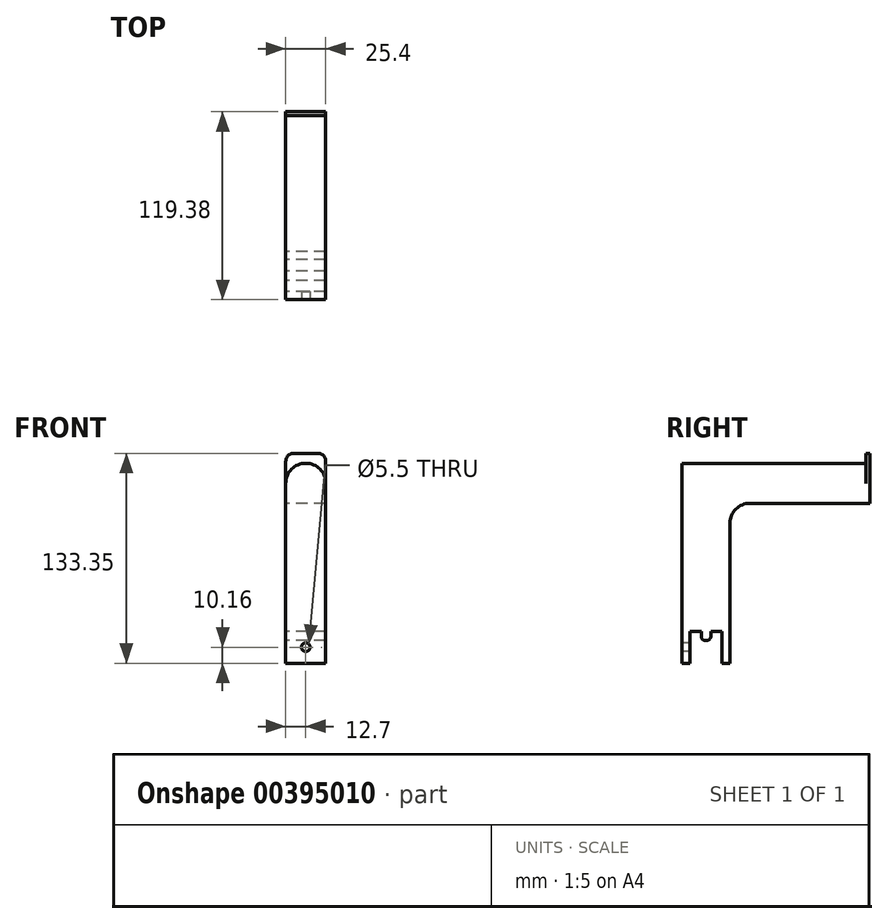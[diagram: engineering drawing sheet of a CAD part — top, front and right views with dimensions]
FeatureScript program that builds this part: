
annotation { "Feature Type Name" : "Feature", "Feature Type Description" : "" }
export const myFeature = defineFeature(function(context is Context, id is Id, definition is map)
    precondition{}
    {
        {
            var Q0;
            Q0=qCreatedBy(makeId("Right.planeOp"),FACE);
            var sketch = newSketch(context, id + "F0", { "sketchPlane" : qUnion([Q0])});
            skLineSegment(sketch, "E0.top", {"start": v(10.16, 10.16) * mm, "end": v(3.05, 10.16) * mm});
            skLineSegment(sketch, "E0.left", {"start": v(10.16, -10.16) * mm, "end": v(10.16, 10.16) * mm});
            skLineSegment(sketch, "E0.right", {"start": v(-10.16, -10.16) * mm, "end": v(-10.16, 10.16) * mm});
            skPoint(sketch, "E0.middle", {"position": v(0, 0) * mm});
            skLineSegment(sketch, "E1", {"start": v(-0.5, 4.32) * mm, "end": v(0.5, 4.32) * mm});
            skLineSegment(sketch, "E2", {"start": v(-3.05, 6.86) * mm, "end": v(-3.05, 10.16) * mm});
            skLineSegment(sketch, "E3", {"start": v(3.05, 6.86) * mm, "end": v(3.05, 10.16) * mm});
            skLineSegment(sketch, "E4.trimOffspring", {"start": v(-3.05, 10.16) * mm, "end": v(-10.16, 10.16) * mm});
            skPoint(sketch, "E5.visualSharp", {"position": v(-3.05, 4.32) * mm});
            skArc(sketch, "E5.filletArc", {"start": v(-3.05, 6.86) * mm, "mid": v(-2.3, 5.06) * mm, "end": v(-0.5, 4.32) * mm});
            skPoint(sketch, "E6.visualSharp", {"position": v(3.05, 4.32) * mm});
            skArc(sketch, "E6.filletArc", {"start": v(0.5, 4.32) * mm, "mid": v(2.3, 5.06) * mm, "end": v(3.05, 6.86) * mm});
            skLineSegment(sketch, "E7", {"start": v(-10.16, -10.16) * mm, "end": v(-15.24, -10.16) * mm});
            skLineSegment(sketch, "E8", {"start": v(10.16, -10.16) * mm, "end": v(15.24, -10.16) * mm});
            skLineSegment(sketch, "E9", {"start": v(-15.24, -10.16) * mm, "end": v(-15.24, 116.84) * mm});
            skLineSegment(sketch, "E10", {"start": v(104.14, 123.19) * mm, "end": v(104.14, 91.44) * mm});
            skLineSegment(sketch, "E11", {"start": v(104.14, 91.44) * mm, "end": v(15.24, 91.44) * mm});
            skLineSegment(sketch, "E12", {"start": v(15.24, 91.44) * mm, "end": v(15.24, -10.16) * mm});
            skLineSegment(sketch, "E13", {"start": v(104.14, 123.19) * mm, "end": v(101.6, 123.19) * mm});
            skLineSegment(sketch, "E14", {"start": v(101.6, 123.19) * mm, "end": v(101.6, 116.84) * mm});
            skLineSegment(sketch, "E15", {"start": v(101.6, 116.84) * mm, "end": v(-15.24, 116.84) * mm});
            skSolve(sketch);
        }
        {
            var Q0;
            Q0=makeQuery(id+"F0.imprint","IMPRINT",FACE,{"disambiguationData":[TD([[makeQuery(id+"F0.imprint","IMPRINT",EDGE,{"derivedFrom":sQuery(id+"F0.wireOp",EDGE,"E0.top")}),-1.0]])]});
            extrude(context, id + "F1", {"entities" : qUnion([Q0]), "depth" : 25.4 * mm});
        }
        {
            var Q0;
            Q0=makeQuery(id+"F1.opExtrude","CAP_EDGE",EDGE,{"disambiguationData":[OSD([sQuery(id+"F0.wireOp",EDGE,"E15")])],"isStart":false});
            var Q1;
            Q1=makeQuery(id+"F1.opExtrude","CAP_EDGE",EDGE,{"disambiguationData":[OSD([sQuery(id+"F0.wireOp",EDGE,"E15")])],"isStart":true});
            fillet(context, id + "F2", {"entities" : qUnion([Q0, Q1]), "radius" : 12.7 * mm, "tangentPropagation" : true, "allowEdgeOverflow" : false});
        }
        {
            var Q0;
            Q0=makeQuery(id+"F1.opExtrude","CAP_EDGE",EDGE,{"disambiguationData":[OSD([sQuery(id+"F0.wireOp",EDGE,"E13")])],"isStart":true});
            var Q1;
            Q1=makeQuery(id+"F1.opExtrude","CAP_EDGE",EDGE,{"disambiguationData":[OSD([sQuery(id+"F0.wireOp",EDGE,"E13")])],"isStart":false});
            fillet(context, id + "F3", {"entities" : qUnion([Q0, Q1]), "radius" : 5.08 * mm, "tangentPropagation" : true, "allowEdgeOverflow" : false});
        }
        {
            var Q0;
            Q0=makeQuery(id+"F1.opExtrude","SWEPT_EDGE",EDGE,{"disambiguationData":[OSD([sQuery(id+"F0.wireOp",EDGE,"E11"),sQuery(id+"F0.wireOp",EDGE,"E12")])]});
            fillet(context, id + "F4", {"entities" : qUnion([Q0]), "radius" : 12.7 * mm, "tangentPropagation" : true, "allowEdgeOverflow" : false});
        }
        {
            var Q0;
            Q0=makeQuery(id+"F1.opExtrude","SWEPT_FACE",FACE,{"disambiguationData":[OSD([sQuery(id+"F0.wireOp",EDGE,"E9")])]});
            var sketch = newSketch(context, id + "F5", { "sketchPlane" : qUnion([Q0])});
            skLineSegment(sketch, "E16", {"start": v(25.4, 0) * mm, "end": v(0, 0) * mm, "construction": true});
            skPoint(sketch, "E17", {"position": v(12.7, 0) * mm});
            skSolve(sketch);
        }
        {
            var Q0;
            Q0=sQuery(id+"F5.wireOp",VERTEX,"E17");
            var Q1;
            Q1=makeQuery(id+"F1.opExtrude","SWEPT_BODY",BODY,{"disambiguationData":[OSD([sQuery(id+"F0.wireOp",EDGE,"E0.top"),sQuery(id+"F0.wireOp",EDGE,"E0.left"),sQuery(id+"F0.wireOp",EDGE,"E0.right"),sQuery(id+"F0.wireOp",EDGE,"E1"),sQuery(id+"F0.wireOp",EDGE,"E2"),sQuery(id+"F0.wireOp",EDGE,"E3"),sQuery(id+"F0.wireOp",EDGE,"E4.trimOffspring"),sQuery(id+"F0.wireOp",EDGE,"E5.filletArc"),sQuery(id+"F0.wireOp",EDGE,"E6.filletArc"),sQuery(id+"F0.wireOp",EDGE,"E7"),sQuery(id+"F0.wireOp",EDGE,"E8"),sQuery(id+"F0.wireOp",EDGE,"E9"),sQuery(id+"F0.wireOp",EDGE,"E10"),sQuery(id+"F0.wireOp",EDGE,"E11"),sQuery(id+"F0.wireOp",EDGE,"E12"),sQuery(id+"F0.wireOp",EDGE,"E13"),sQuery(id+"F0.wireOp",EDGE,"E14"),sQuery(id+"F0.wireOp",EDGE,"E15")])]});
            hole(context, id + "F6", {"style" : HoleStyle.SIMPLE, "endStyle" : HoleEndStyle.BLIND, "standardTappedOrClearance" : lookupTablePath({ "standard" : "ISO", "fit" : "Normal", "size" : "M5", "type" : "Clearance" }), "standardBlindInLast" : lookupTablePath({ "fit" : "Standard", "standard" : "ISO", "size" : "M5", "type" : "Clearance" }), "holeDiameter" : 5.5 * mm, "holeDepth" : 5.6 * mm, "isTappedThrough" : true, "tappedDepth" : 5.6 * mm, "tapClearance" : 0, "startFromSketch" : true, "locations" : qUnion([Q0]), "scope" : qUnion([Q1])});
        }
    });
